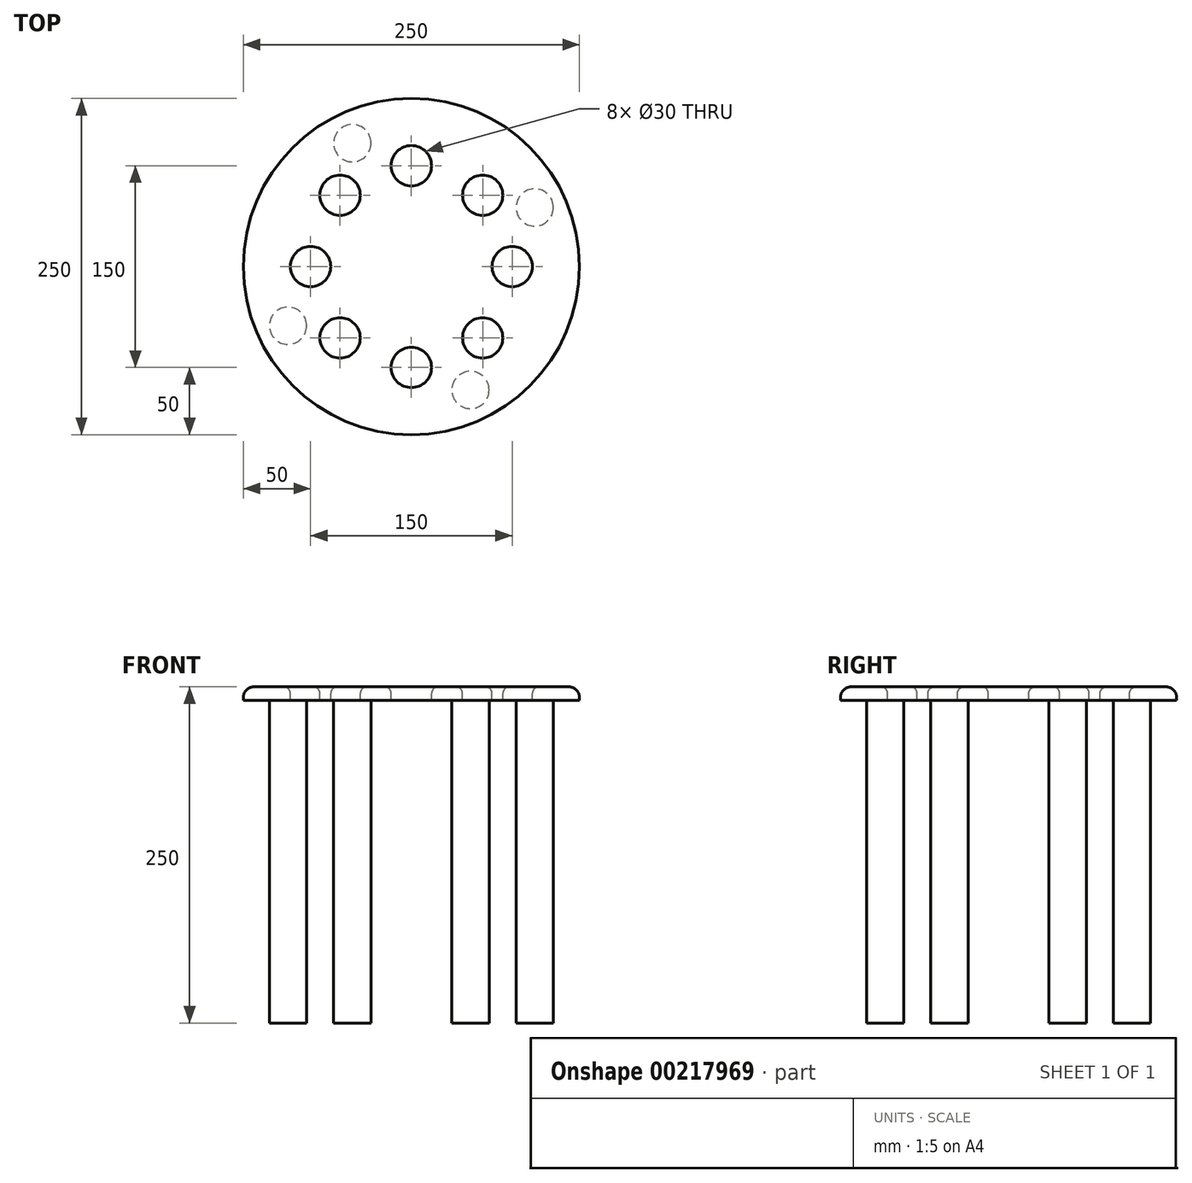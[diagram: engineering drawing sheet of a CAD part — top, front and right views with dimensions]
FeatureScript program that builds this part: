
annotation { "Feature Type Name" : "Feature", "Feature Type Description" : "" }
export const myFeature = defineFeature(function(context is Context, id is Id, definition is map)
    precondition{}
    {
        {
            var Q0;
            Q0=qCreatedBy(makeId("Top.planeOp"),FACE);
            var sketch = newSketch(context, id + "F0", { "sketchPlane" : qUnion([Q0])});
            skCircle(sketch, "E0", {"center": v(0, 0) * mm, "radius": 125 * mm});
            skSolve(sketch);
        }
        {
            var Q0;
            Q0=makeQuery(id+"F0.imprint","IMPRINT",FACE,{"disambiguationData":[TD([[makeQuery(id+"F0.imprint","IMPRINT",EDGE,{"derivedFrom":sQuery(id+"F0.wireOp",EDGE,"E0")}),1.0]])]});
            var sketch = newSketch(context, id + "F1", { "sketchPlane" : qUnion([Q0])});
            skCircle(sketch, "E1", {"center": v(0, 75) * mm, "radius": 15 * mm});
            skCircle(sketch, "E2.1.0", {"center": v(-53.03, 53.03) * mm, "radius": 15 * mm});
            skCircle(sketch, "E2.2.0", {"center": v(-75, 0) * mm, "radius": 15 * mm});
            skCircle(sketch, "E2.3.0", {"center": v(-53.03, -53.03) * mm, "radius": 15 * mm});
            skCircle(sketch, "E2.4.0", {"center": v(0, -75) * mm, "radius": 15 * mm});
            skCircle(sketch, "E2.5.0", {"center": v(53.03, -53.03) * mm, "radius": 15 * mm});
            skCircle(sketch, "E2.6.0", {"center": v(75, 0) * mm, "radius": 15 * mm});
            skCircle(sketch, "E2.7.0", {"center": v(53.03, 53.03) * mm, "radius": 15 * mm});
            skPoint(sketch, "E2.center", {"position": v(0, 0) * mm});
            skSolve(sketch);
        }
        {
            var Q0;
            Q0=makeQuery(id+"F0.imprint","IMPRINT",FACE,{"disambiguationData":[TD([[makeQuery(id+"F0.imprint","IMPRINT",EDGE,{"derivedFrom":sQuery(id+"F0.wireOp",EDGE,"E0")}),1.0]])]});
            extrude(context, id + "F2", {"entities" : qUnion([Q0]), "oppositeDirection" : true, "depth" : 10 * mm});
        }
        {
            var Q0;
            Q0 = qSketchRegion(id + "F1", true);
            extrude(context, id + "F3", {"entities" : qUnion([Q0]), "operationType" : NewBodyOperationType.REMOVE, "oppositeDirection" : true, "depth" : 10 * mm});
        }
        {
            var Q0;
            Q0=makeQuery(id+"F2.opExtrude","CAP_EDGE",EDGE,{"disambiguationData":[OSD([sQuery(id+"F0.wireOp",EDGE,"E0")])],"isStart":true});
            fillet(context, id + "F4", {"entities" : qUnion([Q0]), "radius" : 8 * mm, "tangentPropagation" : true, "allowEdgeOverflow" : false});
        }
        {
            var Q0;
            Q0=makeQuery(id+"F2.opExtrude","CAP_FACE",FACE,{"disambiguationData":[OSD([sQuery(id+"F0.wireOp",EDGE,"E0")])],"isStart":true});
            fillet(context, id + "F5", {"entities" : qUnion([Q0]), "radius" : 5 * mm, "tangentPropagation" : true, "allowEdgeOverflow" : false});
        }
        {
            var Q0;
            Q0=makeQuery(id+"F2.opExtrude","CAP_FACE",FACE,{"disambiguationData":[OSD([sQuery(id+"F0.wireOp",EDGE,"E0")])],"isStart":true});
            var sketch = newSketch(context, id + "F6", { "sketchPlane" : qUnion([Q0])});
            skCircle(sketch, "E3", {"center": v(-43.95, 91.77) * mm, "radius": 13.9 * mm});
            skCircle(sketch, "E4.1.0", {"center": v(-91.77, -43.95) * mm, "radius": 13.9 * mm});
            skCircle(sketch, "E4.2.0", {"center": v(43.95, -91.77) * mm, "radius": 13.9 * mm});
            skCircle(sketch, "E4.3.0", {"center": v(91.77, 43.95) * mm, "radius": 13.9 * mm});
            skPoint(sketch, "E4.center", {"position": v(0, 0) * mm});
            skSolve(sketch);
        }
        {
            var Q0;
            Q0 = qSketchRegion(id + "F6", true);
            extrude(context, id + "F7", {"entities" : qUnion([Q0]), "operationType" : NewBodyOperationType.ADD, "oppositeDirection" : true, "depth" : 250 * mm});
        }
    });
